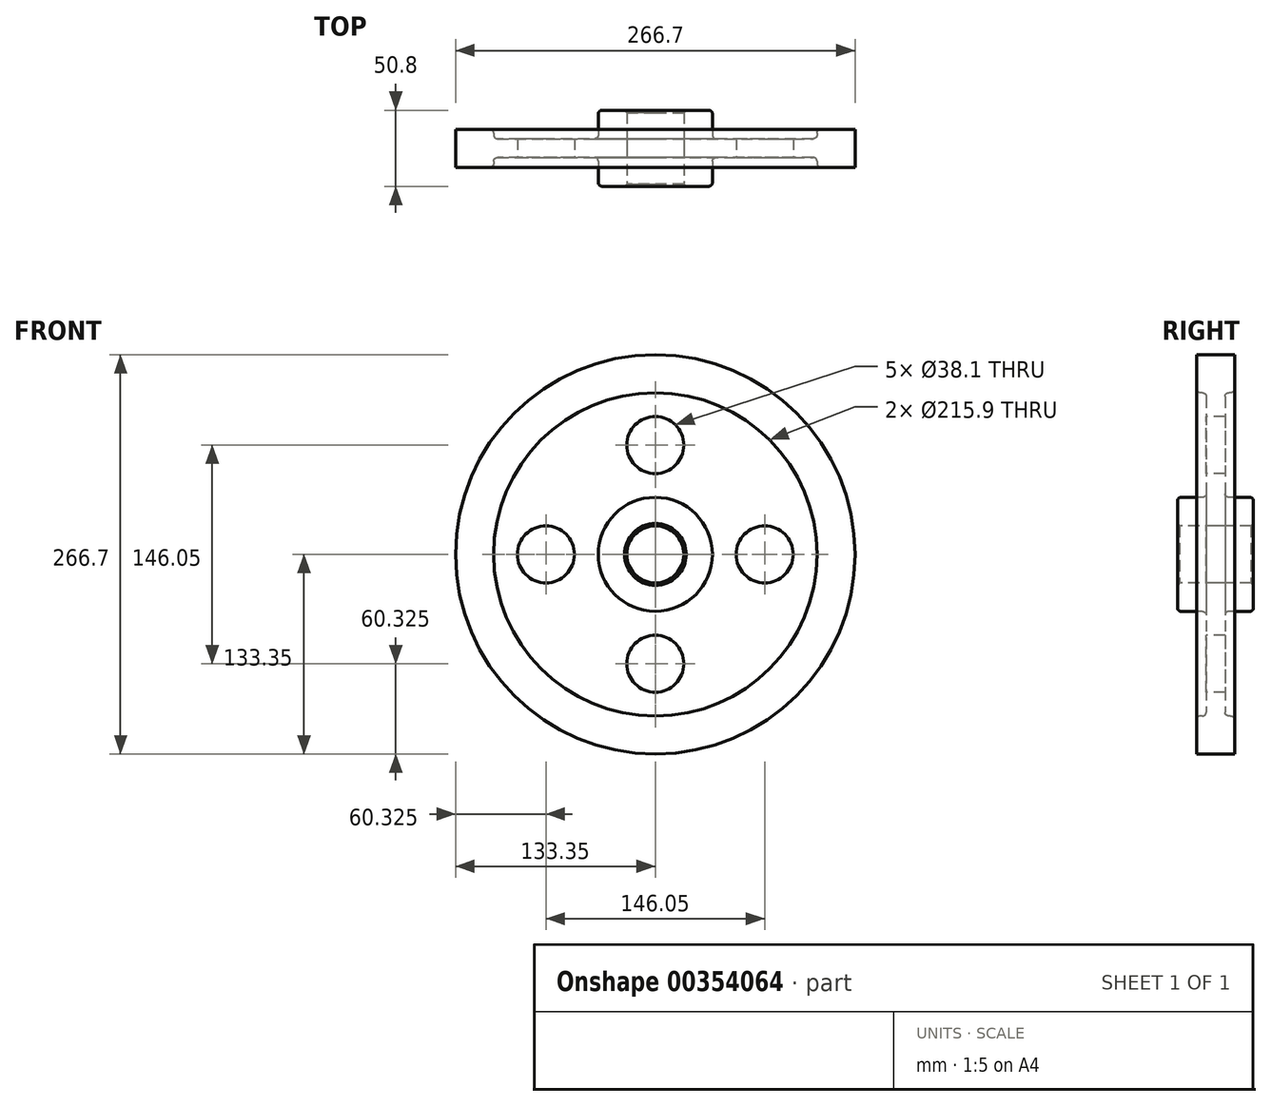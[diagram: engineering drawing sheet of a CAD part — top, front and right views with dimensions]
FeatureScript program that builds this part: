
annotation { "Feature Type Name" : "Feature", "Feature Type Description" : "" }
export const myFeature = defineFeature(function(context is Context, id is Id, definition is map)
    precondition{}
    {
        {
            var Q0;
            Q0=qCreatedBy(makeId("Right.planeOp"),FACE);
            var sketch = newSketch(context, id + "F0", { "sketchPlane" : qUnion([Q0])});
            skLineSegment(sketch, "E0", {"start": v(0, 0) * mm, "end": v(94.54, 0) * mm, "construction": true});
            skLineSegment(sketch, "E1.0", {"start": v(0, 19.05) * mm, "end": v(25.4, 19.05) * mm});
            skLineSegment(sketch, "E2.0", {"start": v(6.13, 38.1) * mm, "end": v(25.4, 38.1) * mm});
            skLineSegment(sketch, "E3.0", {"start": v(6.13, 107.95) * mm, "end": v(12.7, 107.95) * mm});
            skLineSegment(sketch, "E4.0", {"start": v(0, 133.35) * mm, "end": v(12.7, 133.35) * mm});
            skLineSegment(sketch, "E5", {"start": v(0, 133.35) * mm, "end": v(0, 0) * mm, "construction": true});
            skLineSegment(sketch, "E6.0", {"start": v(25.4, 38.1) * mm, "end": v(25.4, 19.05) * mm});
            skLineSegment(sketch, "E7.0", {"start": v(12.7, 133.35) * mm, "end": v(12.7, 107.95) * mm});
            skLineSegment(sketch, "E8.MirrorCS", {"start": v(0, 133.35) * mm, "end": v(-12.7, 133.35) * mm});
            skLineSegment(sketch, "E9.MirrorCS", {"start": v(-12.7, 133.35) * mm, "end": v(-12.7, 107.95) * mm});
            skLineSegment(sketch, "E10.MirrorCS", {"start": v(-6.13, 107.95) * mm, "end": v(-6.13, 38.1) * mm});
            skLineSegment(sketch, "E11.MirrorCS", {"start": v(-6.13, 38.1) * mm, "end": v(-25.4, 38.1) * mm});
            skLineSegment(sketch, "E12.MirrorCS", {"start": v(-25.4, 38.1) * mm, "end": v(-25.4, 19.05) * mm});
            skLineSegment(sketch, "E13.MirrorCS", {"start": v(0, 19.05) * mm, "end": v(-25.4, 19.05) * mm});
            skLineSegment(sketch, "E14.0", {"start": v(6.35, 107.95) * mm, "end": v(6.35, 38.1) * mm});
            skLineSegment(sketch, "E15.MirrorCS", {"start": v(-6.13, 107.95) * mm, "end": v(-12.7, 107.95) * mm});
            skSolve(sketch);
        }
        {
            var Q0;
            Q0=makeQuery(id+"F0.imprint","IMPRINT",FACE,{"disambiguationData":[TD([[makeQuery(id+"F0.imprint","IMPRINT",EDGE,{"derivedFrom":sQuery(id+"F0.wireOp",EDGE,"E1.0")}),1.0]])]});
            var Q1;
            Q1=sQuery(id+"F0.wireOp",EDGE,"E0");
            revolve(context, id + "F1", {"entities" : qUnion([Q0]), "axis" : qUnion([Q1]), "revolveType" : RevolveType.FULL});
        }
        {
            var Q0;
            Q0=makeQuery(id+"F1.opRevolve","SWEPT_FACE",FACE,{"disambiguationData":[OSD([sQuery(id+"F0.wireOp",EDGE,"E10.MirrorCS")])]});
            var sketch = newSketch(context, id + "F2", { "sketchPlane" : qUnion([Q0])});
            skLineSegment(sketch, "E16", {"start": v(0, 0) * mm, "end": v(0, 73.03) * mm});
            skCircle(sketch, "E17", {"center": v(0, 73.03) * mm, "radius": 19.05 * mm});
            skCircle(sketch, "E18.1.0", {"center": v(-73.03, 0) * mm, "radius": 19.05 * mm});
            skCircle(sketch, "E18.2.0", {"center": v(0, -73.03) * mm, "radius": 19.05 * mm});
            skCircle(sketch, "E18.3.0", {"center": v(73.03, 0) * mm, "radius": 19.05 * mm});
            skPoint(sketch, "E18.center", {"position": v(0, 0) * mm});
            skSolve(sketch);
        }
        {
            var Q0;
            Q0=makeQuery(id+"F2.imprint","IMPRINT",FACE,{"disambiguationData":[TD([[makeQuery(id+"F2.imprint","IMPRINT",EDGE,{"derivedFrom":sQuery(id+"F2.wireOp",EDGE,"E18.3.0")}),1.0]])]});
            var Q1;
            Q1=makeQuery(id+"F2.imprint","IMPRINT",FACE,{"disambiguationData":[TD([[makeQuery(id+"F2.imprint","IMPRINT",EDGE,{"derivedFrom":sQuery(id+"F2.wireOp",EDGE,"E18.2.0")}),1.0]])]});
            var Q2;
            Q2=makeQuery(id+"F2.imprint","IMPRINT",FACE,{"disambiguationData":[TD([[makeQuery(id+"F2.imprint","IMPRINT",EDGE,{"derivedFrom":sQuery(id+"F2.wireOp",EDGE,"E18.1.0")}),1.0]])]});
            var Q3;
            Q3=makeQuery(id+"F2.imprint","IMPRINT",FACE,{"disambiguationData":[TD([[makeQuery(id+"F2.imprint","IMPRINT",EDGE,{"derivedFrom":sQuery(id+"F2.wireOp",EDGE,"E17")}),1.0]])]});
            extrude(context, id + "F3", {"entities" : qUnion([Q0, Q1, Q2, Q3]), "operationType" : NewBodyOperationType.REMOVE, "oppositeDirection" : true, "depth" : 25.4 * mm});
        }
        {
            var Q0;
            Q0=makeQuery(id+"F1.opRevolve","SWEPT_EDGE",EDGE,{"disambiguationData":[OSD([sQuery(id+"F0.wireOp",EDGE,"E11.MirrorCS"),sQuery(id+"F0.wireOp",EDGE,"E12.MirrorCS")])]});
            var Q1;
            Q1=makeQuery(id+"F1.opRevolve","SWEPT_EDGE",EDGE,{"disambiguationData":[OSD([sQuery(id+"F0.wireOp",EDGE,"E10.MirrorCS"),sQuery(id+"F0.wireOp",EDGE,"E11.MirrorCS")])]});
            var Q2;
            Q2=makeQuery(id+"F1.opRevolve","SWEPT_EDGE",EDGE,{"disambiguationData":[OSD([sQuery(id+"F0.wireOp",EDGE,"E9.MirrorCS"),sQuery(id+"F0.wireOp",EDGE,"E15.MirrorCS")])]});
            var Q3;
            Q3=makeQuery(id+"F1.opRevolve","SWEPT_EDGE",EDGE,{"disambiguationData":[OSD([sQuery(id+"F0.wireOp",EDGE,"E10.MirrorCS"),sQuery(id+"F0.wireOp",EDGE,"E15.MirrorCS")])]});
            var Q4;
            Q4=makeQuery(id+"F1.opRevolve","SWEPT_EDGE",EDGE,{"disambiguationData":[OSD([sQuery(id+"F0.wireOp",EDGE,"E2.0"),sQuery(id+"F0.wireOp",EDGE,"E6.0")])]});
            var Q5;
            Q5=makeQuery(id+"F1.opRevolve","SWEPT_EDGE",EDGE,{"disambiguationData":[OSD([sQuery(id+"F0.wireOp",EDGE,"E2.0"),sQuery(id+"F0.wireOp",EDGE,"E14.0")])]});
            var Q6;
            Q6=makeQuery(id+"F1.opRevolve","SWEPT_EDGE",EDGE,{"disambiguationData":[OSD([sQuery(id+"F0.wireOp",EDGE,"E3.0"),sQuery(id+"F0.wireOp",EDGE,"E7.0")])]});
            var Q7;
            Q7=makeQuery(id+"F1.opRevolve","SWEPT_EDGE",EDGE,{"disambiguationData":[OSD([sQuery(id+"F0.wireOp",EDGE,"E3.0"),sQuery(id+"F0.wireOp",EDGE,"E14.0")])]});
            fillet(context, id + "F4", {"entities" : qUnion([Q0, Q1, Q2, Q3, Q4, Q5, Q6, Q7]), "radius" : 2.54 * mm, "tangentPropagation" : true, "allowEdgeOverflow" : false});
        }
        {
            var Q0;
            Q0=makeQuery(id+"F1.opRevolve","SWEPT_EDGE",EDGE,{"disambiguationData":[OSD([sQuery(id+"F0.wireOp",EDGE,"E12.MirrorCS"),sQuery(id+"F0.wireOp",EDGE,"E13.MirrorCS")])]});
            var Q1;
            Q1=makeQuery(id+"F1.opRevolve","SWEPT_EDGE",EDGE,{"disambiguationData":[OSD([sQuery(id+"F0.wireOp",EDGE,"E1.0"),sQuery(id+"F0.wireOp",EDGE,"E6.0")])]});
            chamfer(context, id + "F5", {"entities" : qUnion([Q0, Q1]), "width" : 1.59 * mm, "tangentPropagation" : true});
        }
    });
